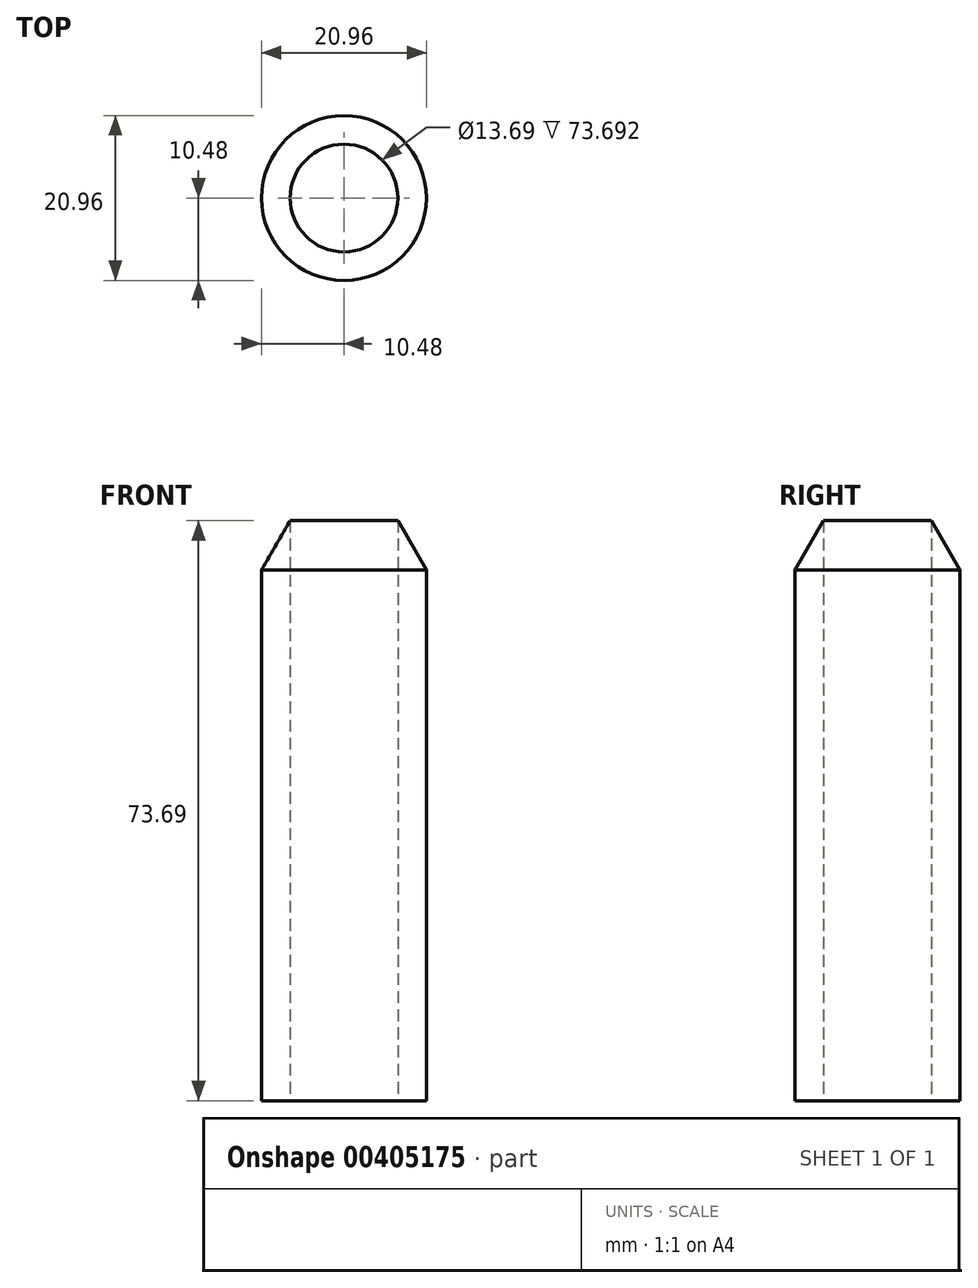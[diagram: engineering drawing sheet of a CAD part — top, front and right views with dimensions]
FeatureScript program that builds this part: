
annotation { "Feature Type Name" : "Feature", "Feature Type Description" : "" }
export const myFeature = defineFeature(function(context is Context, id is Id, definition is map)
    precondition{}
    {
        {
            var Q0;
            Q0=qCreatedBy(makeId("Top.planeOp"),FACE);
            var sketch = newSketch(context, id + "F0", { "sketchPlane" : qUnion([Q0])});
            skCircle(sketch, "E0", {"center": v(0, 0) * mm, "radius": 10.48 * mm});
            skSolve(sketch);
        }
        {
            var Q0;
            Q0=makeQuery(id+"F0.imprint","IMPRINT",FACE,{"disambiguationData":[TD([[makeQuery(id+"F0.imprint","IMPRINT",EDGE,{"derivedFrom":sQuery(id+"F0.wireOp",EDGE,"E0")}),1.0]])]});
            extrude(context, id + "F1", {"entities" : qUnion([Q0]), "depth" : 76.2 * mm});
        }
        {
            var Q0;
            Q0=makeQuery(id+"F1.opExtrude","CAP_EDGE",EDGE,{"disambiguationData":[OSD([sQuery(id+"F0.wireOp",EDGE,"E0")])],"isStart":false});
            chamfer(context, id + "F2", {"entities" : qUnion([Q0]), "chamferType" : ChamferType.OFFSET_ANGLE, "width" : 5.08 * mm, "oppositeDirection" : false, "angle" : 60 * degree, "tangentPropagation" : true});
        }
        {
            var Q0;
            Q0=makeQuery(id+"F1.opExtrude","CAP_FACE",FACE,{"disambiguationData":[OSD([sQuery(id+"F0.wireOp",EDGE,"E0")])],"isStart":true});
            var sketch = newSketch(context, id + "F3", { "sketchPlane" : qUnion([Q0])});
            skCircle(sketch, "E1", {"center": v(0, 0) * mm, "radius": 6.85 * mm});
            skSolve(sketch);
        }
        {
            var Q0;
            Q0=makeQuery(id+"F3.imprint","IMPRINT",FACE,{"disambiguationData":[TD([[makeQuery(id+"F3.imprint","IMPRINT",EDGE,{"derivedFrom":sQuery(id+"F3.wireOp",EDGE,"E1")}),1.0]])]});
            extrude(context, id + "F4", {"entities" : qUnion([Q0]), "operationType" : NewBodyOperationType.REMOVE, "endBound" : BoundingType.THROUGH_ALL, "oppositeDirection" : true, "depth" : 56.64 * mm});
        }
    });
